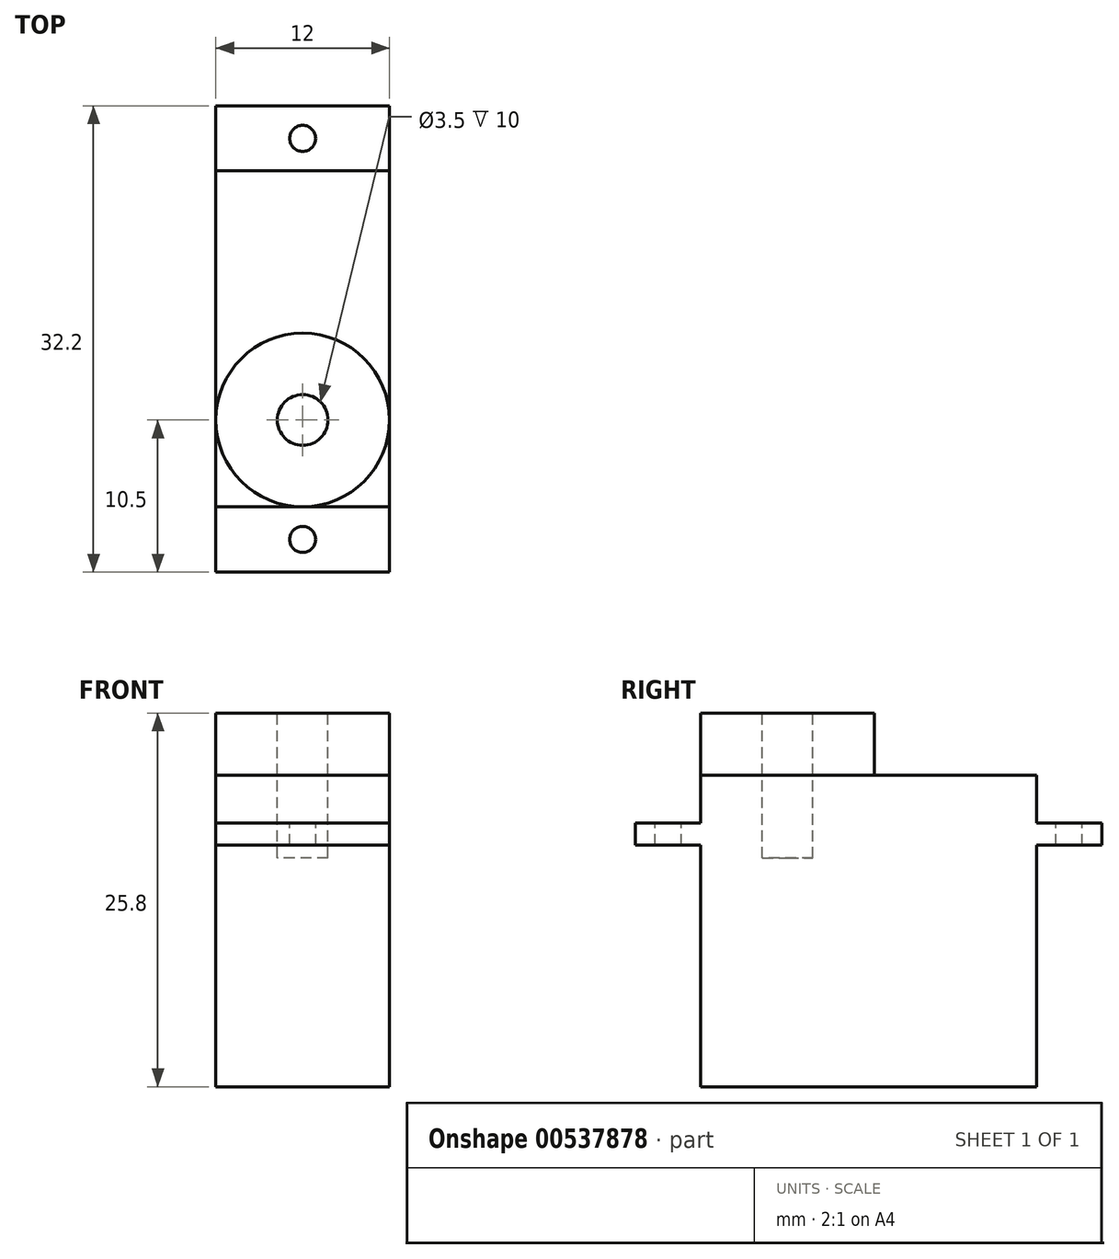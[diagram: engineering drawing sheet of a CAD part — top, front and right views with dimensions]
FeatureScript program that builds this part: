
annotation { "Feature Type Name" : "Feature", "Feature Type Description" : "" }
export const myFeature = defineFeature(function(context is Context, id is Id, definition is map)
    precondition{}
    {
        {
            var Q0;
            Q0=qCreatedBy(makeId("Right.planeOp"),FACE);
            var sketch = newSketch(context, id + "F0", { "sketchPlane" : qUnion([Q0])});
            skLineSegment(sketch, "E0.bottom", {"start": v(0, 21.5) * mm, "end": v(23.2, 21.5) * mm});
            skLineSegment(sketch, "E0.top", {"start": v(0, 0) * mm, "end": v(23.2, 0) * mm});
            skLineSegment(sketch, "E0.left", {"start": v(0, 21.5) * mm, "end": v(0, 0) * mm});
            skLineSegment(sketch, "E0.right", {"start": v(23.2, 21.5) * mm, "end": v(23.2, 0) * mm});
            skLineSegment(sketch, "E1.bottom", {"start": v(23.2, 18.2) * mm, "end": v(27.7, 18.2) * mm});
            skLineSegment(sketch, "E1.top", {"start": v(23.2, 16.7) * mm, "end": v(27.7, 16.7) * mm});
            skLineSegment(sketch, "E1.left", {"start": v(23.2, 18.2) * mm, "end": v(23.2, 16.7) * mm});
            skLineSegment(sketch, "E1.right", {"start": v(27.7, 18.2) * mm, "end": v(27.7, 16.7) * mm});
            skLineSegment(sketch, "E2.bottom", {"start": v(0, 18.2) * mm, "end": v(-4.5, 18.2) * mm});
            skLineSegment(sketch, "E2.top", {"start": v(0, 16.7) * mm, "end": v(-4.5, 16.7) * mm});
            skLineSegment(sketch, "E2.left", {"start": v(0, 18.2) * mm, "end": v(0, 16.7) * mm});
            skLineSegment(sketch, "E2.right", {"start": v(-4.5, 18.2) * mm, "end": v(-4.5, 16.7) * mm});
            skLineSegment(sketch, "E3", {"start": v(0, 18.2) * mm, "end": v(23.2, 18.2) * mm, "construction": true});
            skSolve(sketch);
        }
        {
            var Q0;
            Q0 = qSketchRegion(id + "F0", true);
            extrude(context, id + "F1", {"entities" : qUnion([Q0]), "endBound" : BoundingType.SYMMETRIC, "depth" : 12 * mm, "offsetDistance" : 25 * mm});
        }
        {
            var Q0;
            Q0=makeQuery(id+"F1.opExtrude","SWEPT_FACE",FACE,{"disambiguationData":[OSD([sQuery(id+"F0.wireOp",EDGE,"E2.bottom")])]});
            var sketch = newSketch(context, id + "F2", { "sketchPlane" : qUnion([Q0])});
            skLineSegment(sketch, "E4", {"start": v(0, -4.5) * mm, "end": v(0, 0) * mm, "construction": true});
            skLineSegment(sketch, "E5", {"start": v(0, 23.2) * mm, "end": v(0, 27.7) * mm, "construction": true});
            skPoint(sketch, "E6", {"position": v(0, -2.25) * mm});
            skPoint(sketch, "E7", {"position": v(0, 25.45) * mm});
            skCircle(sketch, "E8", {"center": v(0, -2.25) * mm, "radius": 0.9 * mm});
            skCircle(sketch, "E9", {"center": v(0, 25.45) * mm, "radius": 0.9 * mm});
            skSolve(sketch);
        }
        {
            var Q0;
            Q0=makeQuery(id+"F2.imprint","IMPRINT",FACE,{"disambiguationData":[TD([[makeQuery(id+"F2.imprint","IMPRINT",EDGE,{"derivedFrom":sQuery(id+"F2.wireOp",EDGE,"E8")}),1.0]])]});
            var Q1;
            Q1=makeQuery(id+"F2.imprint","IMPRINT",FACE,{"disambiguationData":[TD([[makeQuery(id+"F2.imprint","IMPRINT",EDGE,{"derivedFrom":sQuery(id+"F2.wireOp",EDGE,"E9")}),1.0]])]});
            extrude(context, id + "F3", {"entities" : qUnion([Q0, Q1]), "operationType" : NewBodyOperationType.REMOVE, "endBound" : BoundingType.THROUGH_ALL, "oppositeDirection" : true, "depth" : 25 * mm, "offsetDistance" : 25 * mm});
        }
        {
            var Q0;
            Q0=makeQuery(id+"F1.opExtrude","SWEPT_FACE",FACE,{"disambiguationData":[OSD([sQuery(id+"F0.wireOp",EDGE,"E0.bottom")])]});
            var sketch = newSketch(context, id + "F4", { "sketchPlane" : qUnion([Q0])});
            skCircle(sketch, "E10", {"center": v(0, 6) * mm, "radius": 6 * mm});
            skSolve(sketch);
        }
        {
            var Q0;
            {var subQ0=sQuery(id+"F4.wireOp",EDGE,"E10");var subQ1=sQuery(id+"F0.wireOp",EDGE,"E0.bottom");var subQ2=makeQuery(id+"F4.imprint","INTERSECT",VERTEX,{"derivedFrom":[makeQuery(id+"F1.opExtrude","CAP_EDGE",EDGE,{"disambiguationData":[OSD([subQ1])],"isStart":true}),subQ0]});Q0=makeQuery(id+"F4.imprint","IMPRINT",FACE,{"disambiguationData":[TD([[makeQuery(id+"F4.imprint","IMPRINT",EDGE,{"disambiguationData":[TD([[subQ2,1.0]])],"derivedFrom":subQ0}),1.0]])]});}
            extrude(context, id + "F5", {"entities" : qUnion([Q0]), "operationType" : NewBodyOperationType.ADD, "depth" : 4.3 * mm, "offsetDistance" : 25 * mm});
        }
        {
            var Q0;
            Q0=makeQuery(id+"F5.opExtrude","CAP_FACE",FACE,{"disambiguationData":[OSD([sQuery(id+"F4.wireOp",EDGE,"E10")])],"isStart":false});
            var sketch = newSketch(context, id + "F6", { "sketchPlane" : qUnion([Q0])});
            skCircle(sketch, "E11", {"center": v(0, 6) * mm, "radius": 1.75 * mm});
            skSolve(sketch);
        }
        {
            var Q0;
            Q0=makeQuery(id+"F6.imprint","IMPRINT",FACE,{"disambiguationData":[TD([[makeQuery(id+"F6.imprint","IMPRINT",EDGE,{"derivedFrom":sQuery(id+"F6.wireOp",EDGE,"E11")}),1.0]])]});
            extrude(context, id + "F7", {"entities" : qUnion([Q0]), "operationType" : NewBodyOperationType.REMOVE, "oppositeDirection" : true, "depth" : 10 * mm, "offsetDistance" : 25 * mm});
        }
    });
